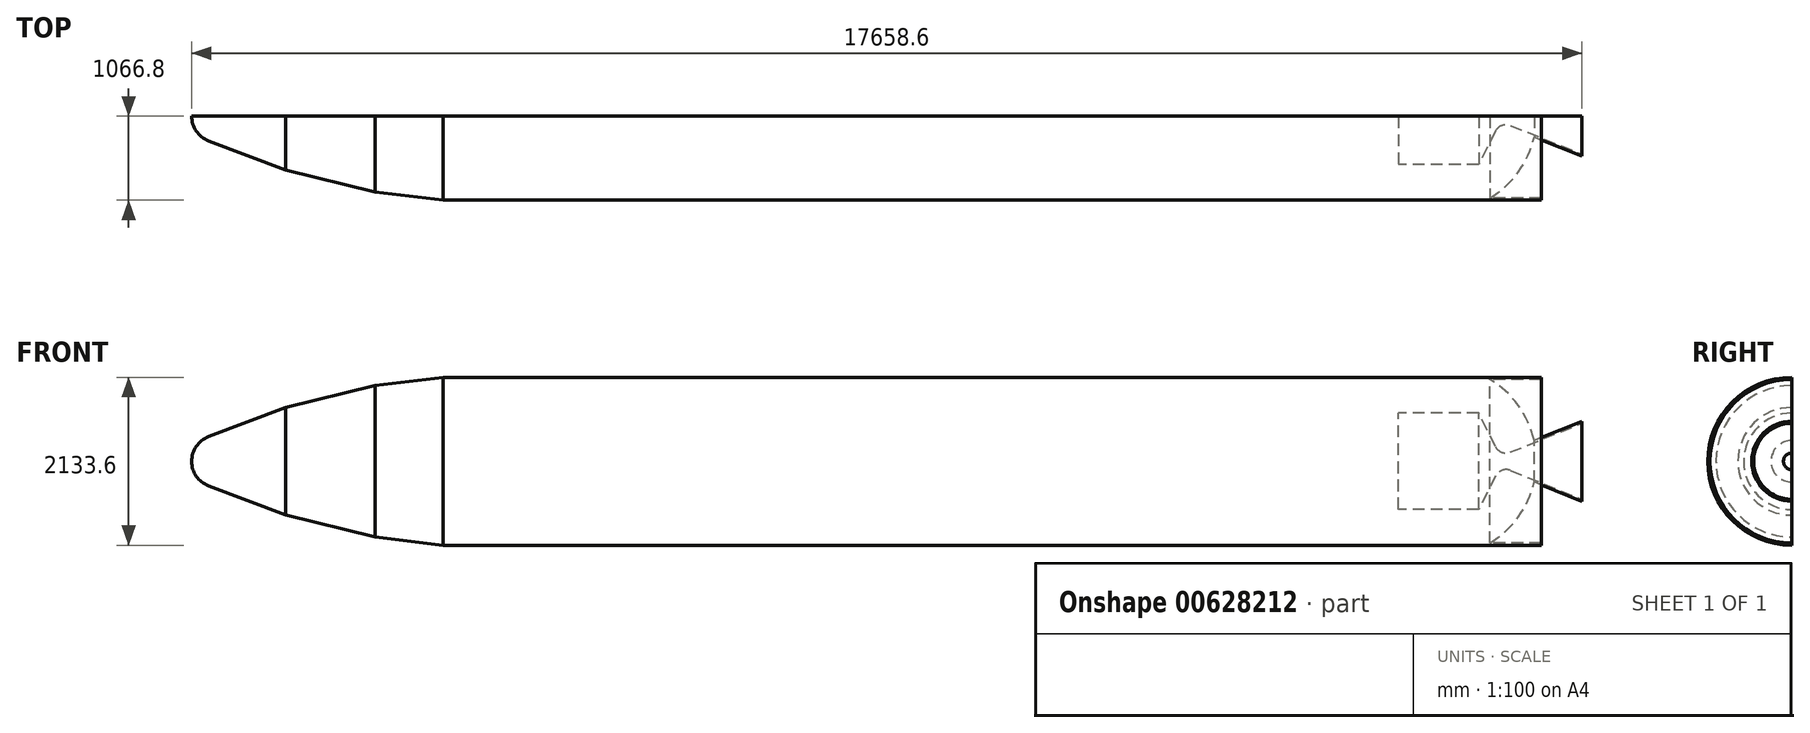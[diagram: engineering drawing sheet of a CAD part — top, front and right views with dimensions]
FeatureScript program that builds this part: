
annotation { "Feature Type Name" : "Feature", "Feature Type Description" : "" }
export const myFeature = defineFeature(function(context is Context, id is Id, definition is map)
    precondition{}
    {
        {
            var Q0;
            Q0=qCreatedBy(makeId("Front.planeOp"),FACE);
            var sketch = newSketch(context, id + "F0", { "sketchPlane" : qUnion([Q0])});
            skLineSegment(sketch, "E0", {"start": v(0, 1066.8) * mm, "end": v(13952.32, 1066.8) * mm});
            skLineSegment(sketch, "E1", {"start": v(13952.32, 1066.8) * mm, "end": v(13952.32, 275.21) * mm, "construction": true});
            skLineSegment(sketch, "E2", {"start": v(0, 1066.8) * mm, "end": v(-864.97, 961.81) * mm});
            skLineSegment(sketch, "E3", {"start": v(-864.97, 961.81) * mm, "end": v(-2002.36, 684.02) * mm});
            skLineSegment(sketch, "E4", {"start": v(-2002.36, 684.02) * mm, "end": v(-2976.95, 312.97) * mm});
            skArc(sketch, "E5", {"start": v(-2976.95, 312.97) * mm, "mid": v(-3133.52, 190.06) * mm, "end": v(-3192.68, 0) * mm});
            skLineSegment(sketch, "E6", {"start": v(-3192.68, 0) * mm, "end": v(-13419.82, 0) * mm, "construction": true});
            skLineSegment(sketch, "E7", {"start": v(13952.32, 0) * mm, "end": v(42473.68, 0) * mm, "construction": true});
            skEllipticalArc(sketch, "E8", {"construction": true});
            skLineSegment(sketch, "E9", {"start": v(42473.68, 0) * mm, "end": v(42473.68, 40933.28) * mm, "construction": true});
            skLineSegment(sketch, "E10", {"start": v(-3192.68, 0) * mm, "end": v(-2738.35, 0) * mm, "construction": true});
            skLineSegment(sketch, "E11", {"start": v(14465.93, 0) * mm, "end": v(14465.93, 508) * mm, "construction": true});
            skLineSegment(sketch, "E12", {"start": v(14465.93, 508) * mm, "end": v(13368.4, 508) * mm, "construction": true});
            skLineSegment(sketch, "E13", {"start": v(13368.4, 343.88) * mm, "end": v(13502.64, 343.88) * mm, "construction": true});
            skLineSegment(sketch, "E14", {"start": v(13502.64, 105.3) * mm, "end": v(13502.64, 0) * mm, "construction": true});
            skArc(sketch, "E15", {"start": v(13502.64, 105.3) * mm, "mid": v(13423.71, 127.75) * mm, "end": v(13368.4, 188.37) * mm});
            skLineSegment(sketch, "E16", {"start": v(13420.42, 105.3) * mm, "end": v(13502.64, 105.3) * mm, "construction": true});
            skArc(sketch, "E17", {"start": v(13502.64, 105.3) * mm, "mid": v(13531.26, 108.06) * mm, "end": v(13558.83, 116.23) * mm});
            skLineSegment(sketch, "E18", {"start": v(13558.83, 116.23) * mm, "end": v(13952.32, 275.21) * mm});
            skLineSegment(sketch, "E19", {"start": v(13368.4, 188.37) * mm, "end": v(13157.3, 611.64) * mm});
            skLineSegment(sketch, "E20", {"start": v(13157.3, 611.64) * mm, "end": v(12136.48, 611.64) * mm});
            skLineSegment(sketch, "E21", {"start": v(12136.48, 611.64) * mm, "end": v(12136.48, 0) * mm});
            skLineSegment(sketch, "E22", {"start": v(12136.48, 0) * mm, "end": v(13504.57, 0) * mm, "construction": true});
            skLineSegment(sketch, "E23", {"start": v(13952.32, 275.21) * mm, "end": v(14465.93, 482.72) * mm});
            skLineSegment(sketch, "E24", {"start": v(13952.32, 275.21) * mm, "end": v(13952.32, 0) * mm, "construction": true});
            skLineSegment(sketch, "E25", {"start": v(13952.32, 1066.8) * mm, "end": v(13952.32, 1039.35) * mm});
            skLineSegment(sketch, "E26", {"start": v(13952.32, 1039.35) * mm, "end": v(13298.26, 1039.35) * mm});
            skArc(sketch, "E27", {"start": v(13298.26, 1039.35) * mm, "mid": v(13659.65, 709.52) * mm, "end": v(13860.7, 263.47) * mm});
            skLineSegment(sketch, "E28", {"start": v(14465.93, 482.72) * mm, "end": v(14465.93, 508) * mm});
            skLineSegment(sketch, "E29", {"start": v(14465.93, 508) * mm, "end": v(13860.7, 263.47) * mm});
            skArc(sketch, "E30", {"start": v(13860.7, 263.47) * mm, "mid": v(13863.24, 251.85) * mm, "end": v(13865.66, 240.2) * mm, "construction": true});
            skLineSegment(sketch, "E31", {"start": v(13504.57, 0) * mm, "end": v(14465.93, 0) * mm, "construction": true});
            skLineSegment(sketch, "E32", {"start": v(12136.48, 0) * mm, "end": v(-3192.68, 0) * mm});
            const initialGuessF0  = {"E8": [58.36481475830078, 0, -1, 0, 71.78463594053545, 41.97470340448322, 4.935610526474175, 0]};
            skSetInitialGuess(sketch, initialGuessF0);
            skSolve(sketch);
        }
        {
            var Q0;
            Q0 = qSketchRegion(id + "F0", true);
            var Q1;
            Q1=sQuery(id+"F0.wireOp",EDGE,"E7");
            revolve(context, id + "F1", {"entities" : qUnion([Q0]), "axis" : qUnion([Q1]), "revolveType" : RevolveType.ONE_DIRECTION, "angle" : 180 * degree});
        }
        {
            var Q0;
            Q0=qCreatedBy(makeId("Front.planeOp"),FACE);
            var sketch = newSketch(context, id + "F2", { "sketchPlane" : qUnion([Q0])});
            skPoint(sketch, "E33.0", {"position": v(13952.32, 1066.8) * mm});
            skPoint(sketch, "E34.0", {"position": v(0, -1066.8) * mm});
            skLineSegment(sketch, "E35", {"start": v(-13419.82, 0) * mm, "end": v(-10559.6, 0) * mm, "construction": true});
            skEllipticalArc(sketch, "E36.MirrorCS", {"construction": true});
            skLineSegment(sketch, "E37", {"start": v(0, 1066.8) * mm, "end": v(-7685.95, 16438.43) * mm});
            skPoint(sketch, "E38.0", {"position": v(0, 1066.8) * mm});
            skEllipticalArc(sketch, "E39.0", {"construction": true});
            skPoint(sketch, "E40.0", {"position": v(-2976.95, 312.97) * mm});
            skLineSegment(sketch, "E41", {"start": v(-2976.95, 312.97) * mm, "end": v(-12751.35, 5715) * mm});
            skLineSegment(sketch, "E42.0", {"start": v(42473.68, 40933.28) * mm, "end": v(42473.68, -40933.28) * mm, "construction": true});
            skPoint(sketch, "E43.0", {"position": v(-2002.36, 684.02) * mm});
            skPoint(sketch, "E44.0", {"position": v(-864.97, 961.81) * mm});
            skLineSegment(sketch, "E45", {"start": v(-2002.36, 684.02) * mm, "end": v(-11652.57, 9256.5) * mm});
            skLineSegment(sketch, "E46", {"start": v(-864.97, 961.81) * mm, "end": v(-9954.17, 12884.66) * mm});
            skLineSegment(sketch, "E47.0", {"start": v(6976.34, 1066.8) * mm, "end": v(0.36, 1066.8) * mm, "construction": true});
            skEllipticalArc(sketch, "E48.0", {"construction": true});
            skEllipticalArc(sketch, "E49", {"construction": true});
            skLineSegment(sketch, "E50", {"start": v(6976.34, 1066.8) * mm, "end": v(13952.32, 1066.8) * mm, "construction": true});
            skLineSegment(sketch, "E51", {"start": v(2972.43, 26698.06) * mm, "end": v(6976.34, 1066.8) * mm});
            skLineSegment(sketch, "E52.0", {"start": v(13952.32, 1039.35) * mm, "end": v(13952.32, 1066.8) * mm, "construction": true});
            skLineSegment(sketch, "E53.0", {"start": v(13860.7, 263.47) * mm, "end": v(14465.93, 508) * mm, "construction": true});
            skLineSegment(sketch, "E54", {"start": v(13952.32, 1066.8) * mm, "end": v(13952.32, 32976.78) * mm});
            skLineSegment(sketch, "E55", {"start": v(14465.93, 508) * mm, "end": v(19112.98, 35143.88) * mm});
            skLineSegment(sketch, "E56", {"start": v(13952.32, 1066.8) * mm, "end": v(42473.68, 9608.45) * mm});
            skLineSegment(sketch, "E57", {"start": v(13952.32, 1039.35) * mm, "end": v(42473.68, 7049.27) * mm});
            skLineSegment(sketch, "E58.0", {"start": v(14465.93, 508) * mm, "end": v(14465.93, 482.72) * mm, "construction": true});
            skLineSegment(sketch, "E59", {"start": v(14465.93, 482.72) * mm, "end": v(42473.68, 4493.39) * mm});
            skLineSegment(sketch, "E60", {"start": v(14465.93, 508) * mm, "end": v(42473.68, 5134.03) * mm});
            skLineSegment(sketch, "E61", {"start": v(14465.93, 482.72) * mm, "end": v(14465.93, 0) * mm});
            skArc(sketch, "E62.0", {"start": v(13558.83, 116.23) * mm, "mid": v(13555.78, 395.6) * mm, "end": v(13368.4, 188.37) * mm, "construction": true});
            skLineSegment(sketch, "E63.0", {"start": v(13502.64, 105.3) * mm, "end": v(13502.64, 0) * mm});
            skLineSegment(sketch, "E64", {"start": v(13952.32, 1039.35) * mm, "end": v(14163.32, 385.74) * mm});
            const initialGuessF2  = {"E36.MirrorCS": [58.36481475830078, 0, -1, 0, 71.78463594053545, 41.97470340448322, 5.880786000752525, 0], "E39.0": [58.36481475830078, 0, -1, 0, 71.78463594053545, 41.97470340448322, 4.935610526474175, 5.290926399295396], "E48.0": [58.36481475830078, 0, -1, 0, 71.78463594053545, 41.97470340448322, 4.935610526474175, 5.593815190525259], "E49": [58.36481475830078, 0, -1, 0, 71.78463594053545, 41.97470340448322, 5.593815190525259, 0]};
            skSetInitialGuess(sketch, initialGuessF2);
            skSolve(sketch);
        }
        {
            var Q0;
            Q0=makeQuery(id+"F1.opRevolve","SWEPT_EDGE",EDGE,{"disambiguationData":[OSD([sQuery(id+"F0.wireOp",EDGE,"E4"),sQuery(id+"F0.wireOp",EDGE,"E5")])]});
            cPoint(context, id + "F3", {"entities" : qUnion([Q0]), "parameter" : 0.5});
        }
        {
            var Q0;
            Q0=makeQuery(id+"F1.opRevolve","CAP_VERTEX",VERTEX,{"disambiguationData":[OSD([sQuery(id+"F0.wireOp",EDGE,"E4"),sQuery(id+"F0.wireOp",EDGE,"E5")])],"isStart":true});
            var Q1;
            Q1=qCreatedBy(id+"F3",VERTEX);
            var Q2;
            Q2=makeQuery(id+"F1.opRevolve","CAP_VERTEX",VERTEX,{"disambiguationData":[OSD([sQuery(id+"F0.wireOp",EDGE,"E4"),sQuery(id+"F0.wireOp",EDGE,"E5")])],"isStart":false});
            cPlane(context, id + "F4", {"entities" : qUnion([Q0, Q1, Q2]), "cplaneType" : CPlaneType.THREE_POINT, "offset" : 25.4 * mm, "width" : 152.4 * mm, "height" : 152.4 * mm});
        }
        {
            var Q0;
            Q0=qCreatedBy(id+"F4.planeOp",FACE);
            cPlane(context, id + "F5", {"entities" : qUnion([Q0]), "cplaneType" : CPlaneType.OFFSET, "offset" : 11430 * mm, "width" : 152.4 * mm, "height" : 152.4 * mm});
        }
        {
            var Q0;
            Q0=qCreatedBy(makeId("Right.planeOp"),FACE);
            cPlane(context, id + "F6", {"entities" : qUnion([Q0]), "cplaneType" : CPlaneType.OFFSET, "offset" : 13502.64 * mm, "width" : 152.4 * mm, "height" : 152.4 * mm});
        }
        {
            var Q0;
            Q0=qCreatedBy(id+"F6.planeOp",FACE);
            cPlane(context, id + "F7", {"entities" : qUnion([Q0]), "cplaneType" : CPlaneType.OFFSET, "offset" : 76.2 * mm, "width" : 152.4 * mm, "height" : 152.4 * mm});
        }
        {
            var Q0;
            Q0=qCreatedBy(id+"F6.planeOp",FACE);
            cPlane(context, id + "F8", {"entities" : qUnion([Q0]), "cplaneType" : CPlaneType.OFFSET, "offset" : 76.2 * mm, "oppositeDirection" : true, "width" : 152.4 * mm, "height" : 152.4 * mm});
        }
        {
            var Q0;
            Q0=qCreatedBy(id+"F6.planeOp",FACE);
            cPlane(context, id + "F9", {"entities" : qUnion([Q0]), "cplaneType" : CPlaneType.OFFSET, "offset" : 29210 * mm, "width" : 152.4 * mm, "height" : 152.4 * mm});
        }
        {
            var Q0;
            Q0=qCreatedBy(makeId("Right.planeOp"),FACE);
            cPlane(context, id + "F10", {"entities" : qUnion([Q0]), "cplaneType" : CPlaneType.OFFSET, "offset" : 12065 * mm, "width" : 152.4 * mm, "height" : 152.4 * mm});
        }
        {
            var Q0;
            Q0=makeQuery(id+"F1.opRevolve","SWEPT_EDGE",EDGE,{"disambiguationData":[OSD([sQuery(id+"F0.wireOp",EDGE,"E19"),sQuery(id+"F0.wireOp",EDGE,"E20")])]});
            cPoint(context, id + "F11", {"entities" : qUnion([Q0]), "parameter" : 0.5});
        }
        {
            var Q0;
            Q0=makeQuery(id+"F1.opRevolve","CAP_VERTEX",VERTEX,{"disambiguationData":[OSD([sQuery(id+"F0.wireOp",EDGE,"E19"),sQuery(id+"F0.wireOp",EDGE,"E20")])],"isStart":true});
            var Q1;
            Q1=qCreatedBy(id+"F11",VERTEX);
            var Q2;
            Q2=makeQuery(id+"F1.opRevolve","CAP_VERTEX",VERTEX,{"disambiguationData":[OSD([sQuery(id+"F0.wireOp",EDGE,"E19"),sQuery(id+"F0.wireOp",EDGE,"E20")])],"isStart":false});
            cPlane(context, id + "F12", {"entities" : qUnion([Q0, Q1, Q2]), "cplaneType" : CPlaneType.THREE_POINT, "offset" : 25.4 * mm, "width" : 152.4 * mm, "height" : 152.4 * mm});
        }
        {
            var Q0;
            Q0=qCreatedBy(id+"F10.planeOp",FACE);
            cPlane(context, id + "F13", {"entities" : qUnion([Q0]), "cplaneType" : CPlaneType.OFFSET, "offset" : 635 * mm, "width" : 152.4 * mm, "height" : 152.4 * mm});
        }
        {
            var Q0;
            Q0=makeQuery(id+"F1.opRevolve","SWEPT_EDGE",EDGE,{"disambiguationData":[OSD([sQuery(id+"F0.wireOp",EDGE,"E23"),sQuery(id+"F0.wireOp",EDGE,"E28")])]});
            cPoint(context, id + "F14", {"entities" : qUnion([Q0]), "parameter" : 0.5});
        }
        {
            var Q0;
            Q0=makeQuery(id+"F1.opRevolve","CAP_VERTEX",VERTEX,{"disambiguationData":[OSD([sQuery(id+"F0.wireOp",EDGE,"E23"),sQuery(id+"F0.wireOp",EDGE,"E28")])],"isStart":false});
            var Q1;
            Q1=qCreatedBy(id+"F14",VERTEX);
            var Q2;
            Q2=makeQuery(id+"F1.opRevolve","CAP_VERTEX",VERTEX,{"disambiguationData":[OSD([sQuery(id+"F0.wireOp",EDGE,"E23"),sQuery(id+"F0.wireOp",EDGE,"E28")])],"isStart":true});
            cPlane(context, id + "F15", {"entities" : qUnion([Q0, Q1, Q2]), "cplaneType" : CPlaneType.THREE_POINT, "offset" : 25.4 * mm, "width" : 152.4 * mm, "height" : 152.4 * mm});
        }
        {
            var Q0;
            Q0=qCreatedBy(id+"F15.planeOp",FACE);
            cPlane(context, id + "F16", {"entities" : qUnion([Q0]), "cplaneType" : CPlaneType.OFFSET, "offset" : 7620 * mm, "width" : 152.4 * mm, "height" : 152.4 * mm});
        }
        {
            var Q0;
            Q0=sQuery(id+"F0.wireOp",EDGE,"E6");
            cPlane(context, id + "F17", {"entities" : qUnion([Q0]), "cplaneType" : CPlaneType.LINE_ANGLE, "offset" : 25.4 * mm, "angle" : 315 * degree, "width" : 152.4 * mm, "height" : 152.4 * mm});
        }
        {
            var Q0;
            Q0=sQuery(id+"F0.wireOp",EDGE,"E6");
            cPlane(context, id + "F18", {"entities" : qUnion([Q0]), "cplaneType" : CPlaneType.LINE_ANGLE, "offset" : 25.4 * mm, "angle" : 45 * degree, "width" : 152.4 * mm, "height" : 152.4 * mm});
        }
    });
